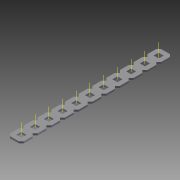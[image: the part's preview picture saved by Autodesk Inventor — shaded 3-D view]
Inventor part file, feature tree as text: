
AUTODESK INVENTOR PART (.ipt)
format: ipt  version: 2015 (Build 190159000, 159)  size: 1,142,784 bytes
history: native  units: in
note: dims shown in document units (in); Inventor stores cm internally (conversion verified against a paired STEP export)
features: other x20, extrude x2, pattern_linear x1, imported_body x1
ambient origin geometry x8: Origin, YZ Plane, XZ Plane, XY Plane, X Axis, Y Axis, Z Axis, Center Point
bodies: Body1 (feature_tree)
feature tree (24):
  other  "Diamond-Pattern"
  other  "Plate"
  extrude  "length cut"  TaperAngle=0.0deg  [1 undecoded]
  extrude  "width cut"  TaperAngle=0.0deg  [1 undecoded]
  other  "constraint axis"
  pattern_linear  "constraint axes"  Spacing1=0.5in  [1 undecoded]
  other  "front plane"
  other  "right plane"
  imported_body  "Base1"
  other  "length profile"
  other  "width profile"
  other  "Work Point1"
  other  "back plane"
  other  "left plane"
  other  "Work Axis170"
  other  "Work Axis171"
  other  "Work Axis172"
  other  "Work Axis173"
  other  "Work Axis174"
  other  "Work Axis175"
  other  "Work Axis176"
  other  "Work Axis177"
  other  "Work Axis178"
  other  "Work Axis229"
note: 3 required parameter values undecoded (feature->parameter linkage not recoverable at this tier; creation-order binding heuristic only, values carry confidence <= 0.55)
